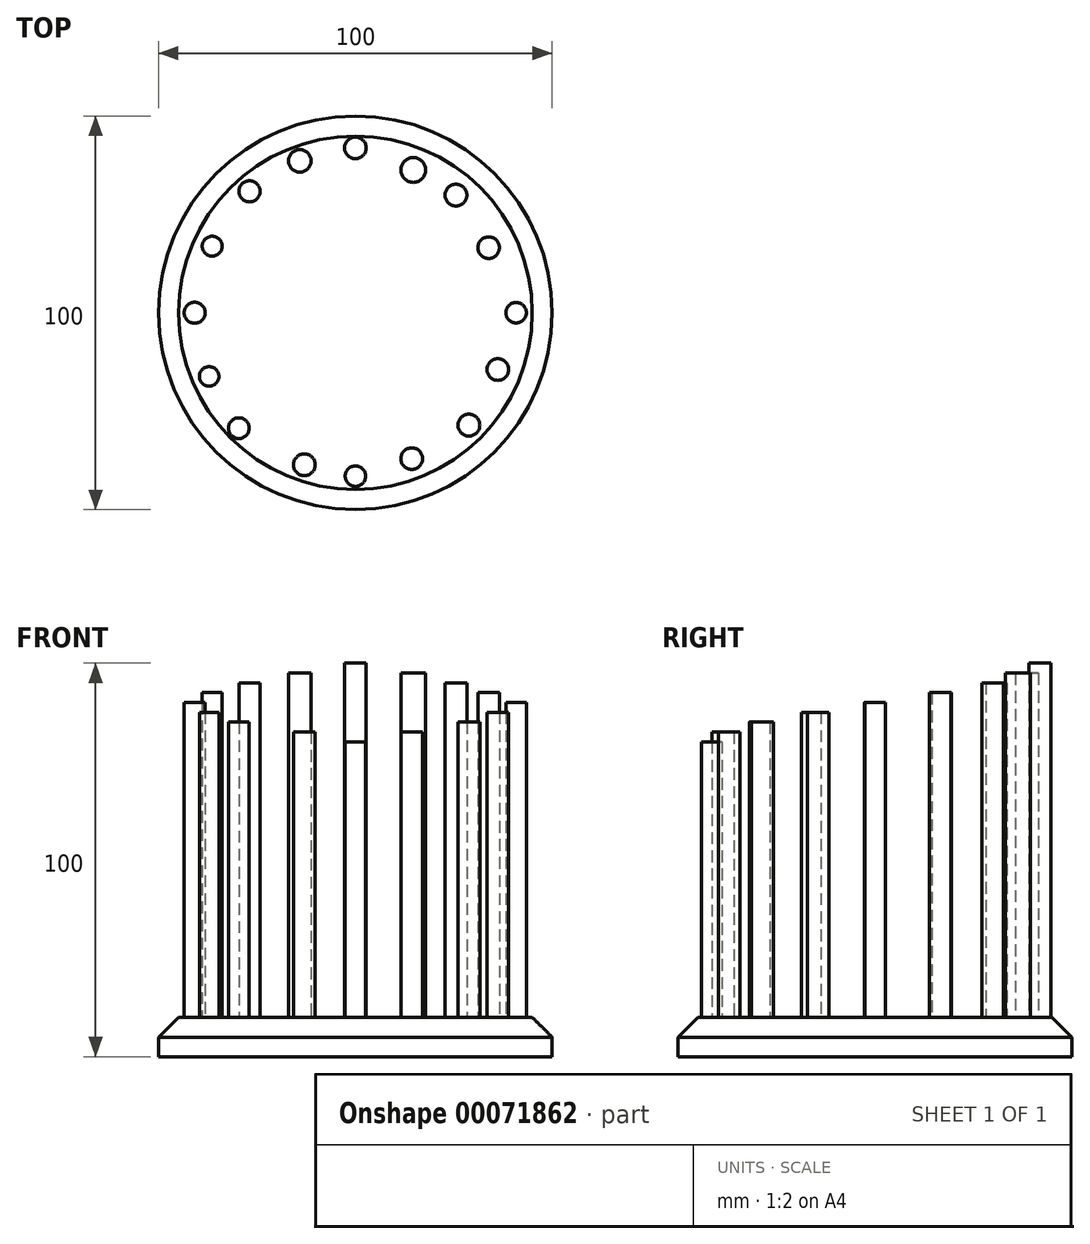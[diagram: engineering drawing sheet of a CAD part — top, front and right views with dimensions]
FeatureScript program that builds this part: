
annotation { "Feature Type Name" : "Feature", "Feature Type Description" : "" }
export const myFeature = defineFeature(function(context is Context, id is Id, definition is map)
    precondition{}
    {
        {
            var Q0;
            Q0=qCreatedBy(makeId("Top.planeOp"),FACE);
            var sketch = newSketch(context, id + "F0", { "sketchPlane" : qUnion([Q0])});
            skCircle(sketch, "E0", {"center": v(0, 0) * mm, "radius": 50 * mm});
            skCircle(sketch, "E1", {"center": v(0, 0) * mm, "radius": 46.58 * mm});
            skCircle(sketch, "E2", {"center": v(0, 41.9) * mm, "radius": 2.75 * mm});
            skCircle(sketch, "E3", {"center": v(0, -41.5) * mm, "radius": 2.6 * mm});
            skCircle(sketch, "E4", {"center": v(40.83, 0) * mm, "radius": 2.6 * mm});
            skCircle(sketch, "E5", {"center": v(-40.83, 0) * mm, "radius": 2.67 * mm});
            skCircle(sketch, "E6", {"center": v(-26.9, 30.87) * mm, "radius": 2.69 * mm});
            skCircle(sketch, "E7", {"center": v(-29.6, -29.32) * mm, "radius": 2.63 * mm});
            skCircle(sketch, "E8", {"center": v(28.83, -28.54) * mm, "radius": 2.77 * mm});
            skCircle(sketch, "E9", {"center": v(25.54, 29.9) * mm, "radius": 2.77 * mm});
            skCircle(sketch, "E10", {"center": v(-36.38, 16.93) * mm, "radius": 2.52 * mm});
            skCircle(sketch, "E11", {"center": v(-14.13, 38.6) * mm, "radius": 2.88 * mm});
            skCircle(sketch, "E12", {"center": v(14.7, 36.28) * mm, "radius": 3.15 * mm});
            skCircle(sketch, "E13", {"center": v(33.86, 16.55) * mm, "radius": 2.74 * mm});
            skCircle(sketch, "E14", {"center": v(36.19, -14.42) * mm, "radius": 2.75 * mm});
            skCircle(sketch, "E15", {"center": v(14.32, -37.06) * mm, "radius": 2.75 * mm});
            skCircle(sketch, "E16", {"center": v(-12.97, -38.6) * mm, "radius": 2.77 * mm});
            skCircle(sketch, "E17", {"center": v(-37.15, -16.16) * mm, "radius": 2.48 * mm});
            skSolve(sketch);
        }
        {
            var Q0;
            Q0=makeQuery(id+"F0.imprint","IMPRINT",FACE,{"disambiguationData":[TD([[makeQuery(id+"F0.imprint","IMPRINT",EDGE,{"derivedFrom":sQuery(id+"F0.wireOp",EDGE,"E0")}),1.0]])]});
            var Q1;
            Q1=makeQuery(id+"F0.imprint","IMPRINT",FACE,{"disambiguationData":[TD([[makeQuery(id+"F0.imprint","IMPRINT",EDGE,{"derivedFrom":sQuery(id+"F0.wireOp",EDGE,"E1")}),1.0]])]});
            extrude(context, id + "F1", {"entities" : qUnion([Q0, Q1]), "depth" : 10 * mm});
        }
        {
            var Q0;
            Q0=makeQuery(id+"F1.opExtrude","CAP_EDGE",EDGE,{"disambiguationData":[OSD([sQuery(id+"F0.wireOp",EDGE,"E0")])],"isStart":false});
            chamfer(context, id + "F2", {"entities" : qUnion([Q0]), "width" : 5.08 * mm, "tangentPropagation" : true});
        }
        {
            var Q0;
            Q0=makeQuery(id+"F0.imprint","IMPRINT",FACE,{"disambiguationData":[TD([[makeQuery(id+"F0.imprint","IMPRINT",EDGE,{"derivedFrom":sQuery(id+"F0.wireOp",EDGE,"E2")}),1.0]])]});
            extrude(context, id + "F3", {"entities" : qUnion([Q0]), "operationType" : NewBodyOperationType.ADD, "depth" : 100 * mm});
        }
        {
            var Q0;
            Q0=makeQuery(id+"F0.imprint","IMPRINT",FACE,{"disambiguationData":[TD([[makeQuery(id+"F0.imprint","IMPRINT",EDGE,{"derivedFrom":sQuery(id+"F0.wireOp",EDGE,"E11")}),1.0]])]});
            var Q1;
            Q1=makeQuery(id+"F0.imprint","IMPRINT",FACE,{"disambiguationData":[TD([[makeQuery(id+"F0.imprint","IMPRINT",EDGE,{"derivedFrom":sQuery(id+"F0.wireOp",EDGE,"E12")}),1.0]])]});
            extrude(context, id + "F4", {"entities" : qUnion([Q0, Q1]), "operationType" : NewBodyOperationType.ADD, "depth" : 97.5 * mm});
        }
        {
            var Q0;
            Q0=makeQuery(id+"F0.imprint","IMPRINT",FACE,{"disambiguationData":[TD([[makeQuery(id+"F0.imprint","IMPRINT",EDGE,{"derivedFrom":sQuery(id+"F0.wireOp",EDGE,"E6")}),1.0]])]});
            var Q1;
            Q1=makeQuery(id+"F0.imprint","IMPRINT",FACE,{"disambiguationData":[TD([[makeQuery(id+"F0.imprint","IMPRINT",EDGE,{"derivedFrom":sQuery(id+"F0.wireOp",EDGE,"E9")}),1.0]])]});
            extrude(context, id + "F5", {"entities" : qUnion([Q0, Q1]), "operationType" : NewBodyOperationType.ADD, "depth" : 95 * mm});
        }
        {
            var Q0;
            Q0=makeQuery(id+"F0.imprint","IMPRINT",FACE,{"disambiguationData":[TD([[makeQuery(id+"F0.imprint","IMPRINT",EDGE,{"derivedFrom":sQuery(id+"F0.wireOp",EDGE,"E10")}),1.0]])]});
            var Q1;
            Q1=makeQuery(id+"F0.imprint","IMPRINT",FACE,{"disambiguationData":[TD([[makeQuery(id+"F0.imprint","IMPRINT",EDGE,{"derivedFrom":sQuery(id+"F0.wireOp",EDGE,"E13")}),1.0]])]});
            extrude(context, id + "F6", {"entities" : qUnion([Q0, Q1]), "operationType" : NewBodyOperationType.ADD, "depth" : 92.5 * mm});
        }
        {
            var Q0;
            Q0=makeQuery(id+"F0.imprint","IMPRINT",FACE,{"disambiguationData":[TD([[makeQuery(id+"F0.imprint","IMPRINT",EDGE,{"derivedFrom":sQuery(id+"F0.wireOp",EDGE,"E4")}),1.0]])]});
            var Q1;
            Q1=makeQuery(id+"F0.imprint","IMPRINT",FACE,{"disambiguationData":[TD([[makeQuery(id+"F0.imprint","IMPRINT",EDGE,{"derivedFrom":sQuery(id+"F0.wireOp",EDGE,"E5")}),1.0]])]});
            extrude(context, id + "F7", {"entities" : qUnion([Q0, Q1]), "operationType" : NewBodyOperationType.ADD, "depth" : 90 * mm});
        }
        {
            var Q0;
            Q0=makeQuery(id+"F0.imprint","IMPRINT",FACE,{"disambiguationData":[TD([[makeQuery(id+"F0.imprint","IMPRINT",EDGE,{"derivedFrom":sQuery(id+"F0.wireOp",EDGE,"E17")}),1.0]])]});
            var Q1;
            Q1=makeQuery(id+"F0.imprint","IMPRINT",FACE,{"disambiguationData":[TD([[makeQuery(id+"F0.imprint","IMPRINT",EDGE,{"derivedFrom":sQuery(id+"F0.wireOp",EDGE,"E14")}),1.0]])]});
            extrude(context, id + "F8", {"entities" : qUnion([Q0, Q1]), "operationType" : NewBodyOperationType.ADD, "depth" : 87.5 * mm});
        }
        {
            var Q0;
            Q0=makeQuery(id+"F0.imprint","IMPRINT",FACE,{"disambiguationData":[TD([[makeQuery(id+"F0.imprint","IMPRINT",EDGE,{"derivedFrom":sQuery(id+"F0.wireOp",EDGE,"E8")}),1.0]])]});
            var Q1;
            Q1=makeQuery(id+"F0.imprint","IMPRINT",FACE,{"disambiguationData":[TD([[makeQuery(id+"F0.imprint","IMPRINT",EDGE,{"derivedFrom":sQuery(id+"F0.wireOp",EDGE,"E7")}),1.0]])]});
            extrude(context, id + "F9", {"entities" : qUnion([Q0, Q1]), "operationType" : NewBodyOperationType.ADD, "depth" : 85 * mm});
        }
        {
            var Q0;
            Q0=makeQuery(id+"F0.imprint","IMPRINT",FACE,{"disambiguationData":[TD([[makeQuery(id+"F0.imprint","IMPRINT",EDGE,{"derivedFrom":sQuery(id+"F0.wireOp",EDGE,"E15")}),1.0]])]});
            var Q1;
            Q1=makeQuery(id+"F0.imprint","IMPRINT",FACE,{"disambiguationData":[TD([[makeQuery(id+"F0.imprint","IMPRINT",EDGE,{"derivedFrom":sQuery(id+"F0.wireOp",EDGE,"E16")}),1.0]])]});
            extrude(context, id + "F10", {"entities" : qUnion([Q0, Q1]), "operationType" : NewBodyOperationType.ADD, "depth" : 82.5 * mm});
        }
        {
            var Q0;
            Q0=makeQuery(id+"F0.imprint","IMPRINT",FACE,{"disambiguationData":[TD([[makeQuery(id+"F0.imprint","IMPRINT",EDGE,{"derivedFrom":sQuery(id+"F0.wireOp",EDGE,"E3")}),1.0]])]});
            extrude(context, id + "F11", {"entities" : qUnion([Q0]), "operationType" : NewBodyOperationType.ADD, "depth" : 80 * mm});
        }
    });
